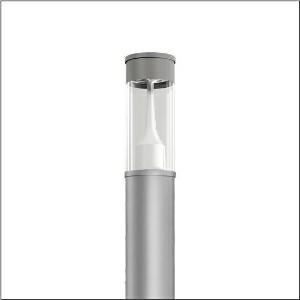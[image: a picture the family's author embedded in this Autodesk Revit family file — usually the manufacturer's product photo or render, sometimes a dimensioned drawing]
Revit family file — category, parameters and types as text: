
# Revit family: city-light_260_iq___pl1_2s_5xa5295cf14h_efd3
name_source: partatom
category: Lighting Fixtures
units: mm (PartAtom-declared; Revit-internal decimal feet)

## family parameters
Cut with Voids When Loaded = No
Host = Face
Light Source = No
Part Type = Normal
Room Calculation Point = No
Round Connector Dimension = Use Diameter
Shared = No

## types (1)
- --- (1 x LED, 2970 lm, 23.9 W, 2200K)
    Apparent Load = 24 VA
    CIE Flux Codes = 23 62 94 96 100
    Color Rendering = 70
    Color Temperature = 2200K
    Default Elevation = 1800 mm
    Description = City-Light 260 iQ, light pillar, Module 540 iQ-SR, primary light control with 3 zone facetted reflector, of plastic, silver coated, highly specular, structured, primary optical cover: cover, of PMMA, transparent, partly coated, light distribution: PL1.2s, primary light characteristic: symmetric, LED, High Power LED, rated luminous flux: 2.970lm, luminous efficacy: 124lm/W, light colour: 722, colour temperature: 2200K, control gear: iQ Street-Remote, control: pre-setting: logarithmic dimming characteristic, Street-Remote, Auto-Match, Temp-Guard, Lumen-Switch, Night-Set, Smart-Wire, Light-Fading, Desk-Remote (wireless, voltage-free reading and setting of iQ features in the workshop via application-optimized NFC function/RFID function), optimised constant luminous flux control (CLO 2.0), with terminal, 6-pole, max. 2.5mm², mains connection: 230..240V, AC, 50/60Hz, start of lifetime: 24W, end of service life: 26W, reduction: 12W, luminaire housing, cylindrical, of extruded aluminium section, coated, Siteco® metallic grey (DB 702S), length: 2.600mm, diameter: 200mm, Module 540 iQ-SR, traffic white (RAL 9016), equipment: standard, protection rating (complete): IP65, insulation class (complete): insulation class II (safety insulation), certification: CE, ENEC, VDE, packaging unit: 1 piece

Light Distribution: PL1.2s
    Height = 500 mm
    Lamp = 1 x LED
    Lamp Light Flux = 2970 lm
    Lamp Power = 23.9 W
    Lamp count = 1
    Length = 200 mm  [stored 0.656168 ft]
    Luminous efficacy = 124 lm/W
    Manufacturer = Siteco
    ModVariant = No
    Model = 5XA5295CF14H
    Mounting Place = Floor
    Mounting Type = Freestanding
    Number of Poles = 1
    OnlyDefault = Yes
    Power Factor = 1
    Product Name = City-Light 260 iQ | PL1.2s
    Product group = light pillar
    ProductGroupID = 1301
    Protection Class = Protection class II
    Protection Degree = IP 65
    RLX_Detail_Level = 1
    RLX_Emergency_Light_Flux = 0 lm
    RLX_Emergency_Type = 0
    RLX_Emergency_Type_DB = No
    RlxData = <blob elided: 22005 chars, md5=8286070d>
    Socket = socket
    Standby Power = 0 W
    System Light Flux = 2970 lm
    System Power = 24 W
    Type Comments = factory setting: luminous flux: 100 % | dim-lin: 254 | 499 mA
    Type Image = l_1006920.jpg
    URL = http://relux.com
    VarID = @adj_166563
    Voltage = 0 V
    Weight = 0.00 kg
    Width = 0 mm  [stored 0 ft]

note: [stored X ft] marks values corroborated as IEEE doubles in the binary element streams (Revit-internal decimal feet)

## geometry (parser evidence)
native form markers: Blend x4, Sweep x12
no freeform markers — native parametric forms only
